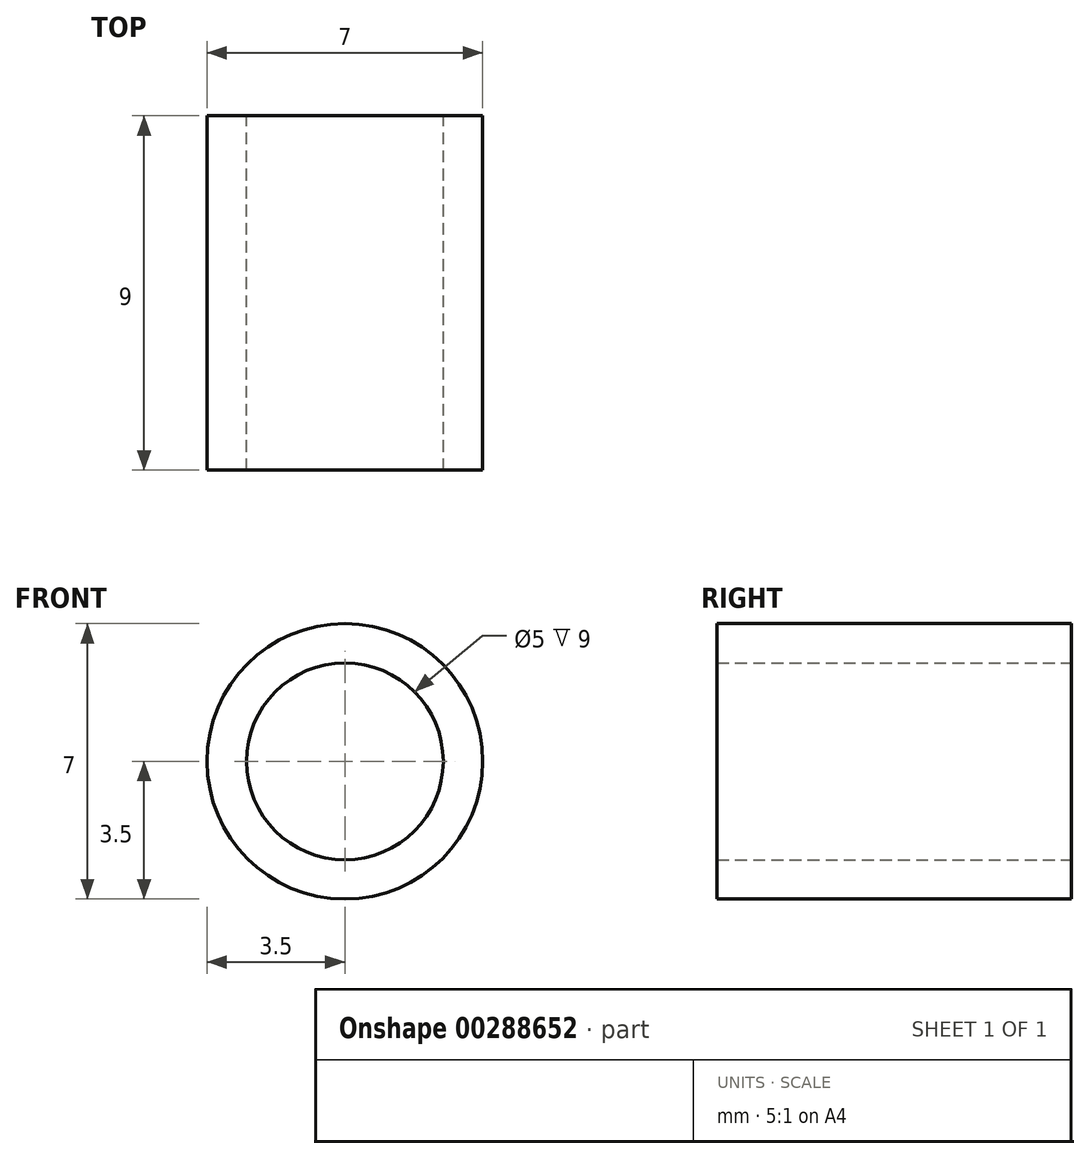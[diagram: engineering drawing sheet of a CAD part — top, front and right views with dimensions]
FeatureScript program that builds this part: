
annotation { "Feature Type Name" : "Feature", "Feature Type Description" : "" }
export const myFeature = defineFeature(function(context is Context, id is Id, definition is map)
    precondition{}
    {
        {
            var Q0;
            Q0=qCreatedBy(makeId("Front.planeOp"),FACE);
            var sketch = newSketch(context, id + "F0", { "sketchPlane" : qUnion([Q0])});
            skCircle(sketch, "E0", {"center": v(0, 0) * mm, "radius": 2.5 * mm});
            skCircle(sketch, "E1", {"center": v(0, 0) * mm, "radius": 3.5 * mm});
            skSolve(sketch);
        }
        {
            var Q0;
            Q0=makeQuery(id+"F0.imprint","IMPRINT",FACE,{"disambiguationData":[TD([[makeQuery(id+"F0.imprint","IMPRINT",EDGE,{"derivedFrom":sQuery(id+"F0.wireOp",EDGE,"E0")}),-1.0]])]});
            extrude(context, id + "F1", {"entities" : qUnion([Q0]), "depth" : 9 * mm, "offsetDistance" : 25 * mm});
        }
    });
